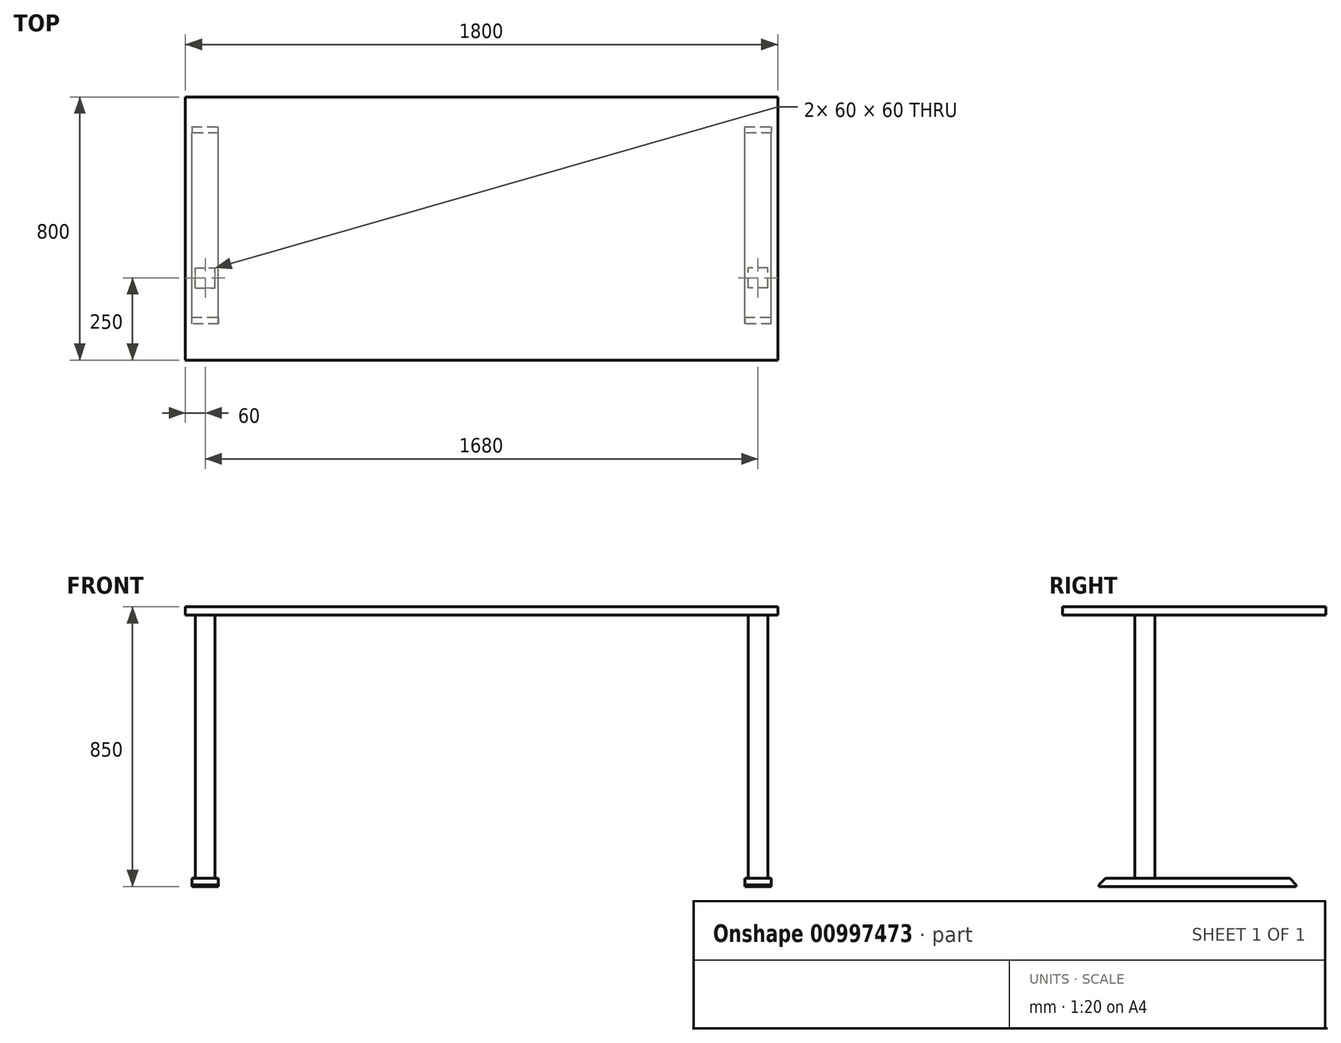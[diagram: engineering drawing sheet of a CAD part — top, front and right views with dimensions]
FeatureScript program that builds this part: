
annotation { "Feature Type Name" : "Feature", "Feature Type Description" : "" }
export const myFeature = defineFeature(function(context is Context, id is Id, definition is map)
    precondition{}
    {
        {
            var Q0;
            Q0=qCreatedBy(makeId("Top.planeOp"),FACE);
            var sketch = newSketch(context, id + "F0", { "sketchPlane" : qUnion([Q0])});
            skLineSegment(sketch, "E0.bottom", {"start": v(0, 0) * mm, "end": v(1800, 0) * mm});
            skLineSegment(sketch, "E0.top", {"start": v(0, -800) * mm, "end": v(1800, -800) * mm});
            skLineSegment(sketch, "E0.left", {"start": v(0, 0) * mm, "end": v(0, -800) * mm});
            skLineSegment(sketch, "E0.right", {"start": v(1800, 0) * mm, "end": v(1800, -800) * mm});
            skSolve(sketch);
        }
        {
            var Q0;
            Q0=makeQuery(id+"F0.imprint","IMPRINT",FACE,{"disambiguationData":[TD([[makeQuery(id+"F0.imprint","IMPRINT",EDGE,{"derivedFrom":sQuery(id+"F0.wireOp",EDGE,"E0.bottom")}),-1.0]])]});
            extrude(context, id + "F1", {"entities" : qUnion([Q0]), "depth" : 25 * mm, "offsetDistance" : 25 * mm});
        }
        {
            var Q0;
            Q0=makeQuery(id+"F1.opExtrude","CAP_FACE",FACE,{"disambiguationData":[OSD([sQuery(id+"F0.wireOp",EDGE,"E0.bottom"),sQuery(id+"F0.wireOp",EDGE,"E0.top"),sQuery(id+"F0.wireOp",EDGE,"E0.left"),sQuery(id+"F0.wireOp",EDGE,"E0.right")])],"isStart":true});
            var sketch = newSketch(context, id + "F2", { "sketchPlane" : qUnion([Q0])});
            skLineSegment(sketch, "E1.bottom", {"start": v(30, 580) * mm, "end": v(90, 580) * mm});
            skLineSegment(sketch, "E1.top", {"start": v(30, 520) * mm, "end": v(90, 520) * mm});
            skLineSegment(sketch, "E1.left", {"start": v(30, 580) * mm, "end": v(30, 520) * mm});
            skLineSegment(sketch, "E1.right", {"start": v(90, 580) * mm, "end": v(90, 520) * mm});
            skLineSegment(sketch, "E2", {"start": v(900, 800) * mm, "end": v(900, 0) * mm, "construction": true});
            skLineSegment(sketch, "E3.MirrorCS", {"start": v(1770, 520) * mm, "end": v(1710, 520) * mm});
            skLineSegment(sketch, "E4.MirrorCS", {"start": v(1770, 580) * mm, "end": v(1710, 580) * mm});
            skLineSegment(sketch, "E5.MirrorCS", {"start": v(1710, 580) * mm, "end": v(1710, 520) * mm});
            skLineSegment(sketch, "E6.MirrorCS", {"start": v(1770, 580) * mm, "end": v(1770, 520) * mm});
            skSolve(sketch);
        }
        {
            var Q0;
            Q0 = qSketchRegion(id + "F2", true);
            extrude(context, id + "F3", {"entities" : qUnion([Q0]), "operationType" : NewBodyOperationType.ADD, "depth" : 800 * mm, "offsetDistance" : 25 * mm});
        }
        {
            var Q0;
            Q0=makeQuery(id+"F3.opExtrude","CAP_FACE",FACE,{"disambiguationData":[OSD([sQuery(id+"F2.wireOp",EDGE,"E1.bottom"),sQuery(id+"F2.wireOp",EDGE,"E1.top"),sQuery(id+"F2.wireOp",EDGE,"E1.left"),sQuery(id+"F2.wireOp",EDGE,"E1.right")])],"isStart":false});
            var sketch = newSketch(context, id + "F4", { "sketchPlane" : qUnion([Q0])});
            skLineSegment(sketch, "E7.bottom", {"start": v(20, 690) * mm, "end": v(100, 690) * mm});
            skLineSegment(sketch, "E7.top", {"start": v(20, 90) * mm, "end": v(100, 90) * mm});
            skLineSegment(sketch, "E7.left", {"start": v(20, 690) * mm, "end": v(20, 90) * mm});
            skLineSegment(sketch, "E7.right", {"start": v(100, 690) * mm, "end": v(100, 90) * mm});
            skLineSegment(sketch, "E8", {"start": v(60, 580) * mm, "end": v(60, 520) * mm, "construction": true});
            skPoint(sketch, "E9.0", {"position": v(900, 800) * mm});
            skLineSegment(sketch, "E10", {"start": v(900, 800) * mm, "end": v(900, 0) * mm, "construction": true});
            skLineSegment(sketch, "E11.MirrorCS", {"start": v(1780, 690) * mm, "end": v(1700, 690) * mm});
            skLineSegment(sketch, "E12.MirrorCS", {"start": v(1740, 580) * mm, "end": v(1740, 520) * mm, "construction": true});
            skLineSegment(sketch, "E13.MirrorCS", {"start": v(1780, 90) * mm, "end": v(1700, 90) * mm});
            skLineSegment(sketch, "E14.MirrorCS", {"start": v(1780, 690) * mm, "end": v(1780, 90) * mm});
            skLineSegment(sketch, "E15.MirrorCS", {"start": v(1700, 690) * mm, "end": v(1700, 90) * mm});
            skSolve(sketch);
        }
        {
            var Q0;
            Q0 = qSketchRegion(id + "F4", true);
            extrude(context, id + "F5", {"entities" : qUnion([Q0]), "operationType" : NewBodyOperationType.ADD, "depth" : 25 * mm, "offsetDistance" : 25 * mm});
        }
        {
            var Q0;
            Q0=makeQuery(id+"F5.opExtrude","CAP_EDGE",EDGE,{"disambiguationData":[OSD([sQuery(id+"F4.wireOp",EDGE,"E13.MirrorCS")])],"isStart":true});
            var Q1;
            Q1=makeQuery(id+"F5.opExtrude","CAP_EDGE",EDGE,{"disambiguationData":[OSD([sQuery(id+"F4.wireOp",EDGE,"E7.top")])],"isStart":true});
            var Q2;
            Q2=makeQuery(id+"F5.opExtrude","CAP_EDGE",EDGE,{"disambiguationData":[OSD([sQuery(id+"F4.wireOp",EDGE,"E7.bottom")])],"isStart":true});
            var Q3;
            Q3=makeQuery(id+"F5.opExtrude","CAP_EDGE",EDGE,{"disambiguationData":[OSD([sQuery(id+"F4.wireOp",EDGE,"E11.MirrorCS")])],"isStart":true});
            chamfer(context, id + "F6", {"entities" : qUnion([Q0, Q1, Q2, Q3]), "width" : 20 * mm, "tangentPropagation" : true});
        }
    });
